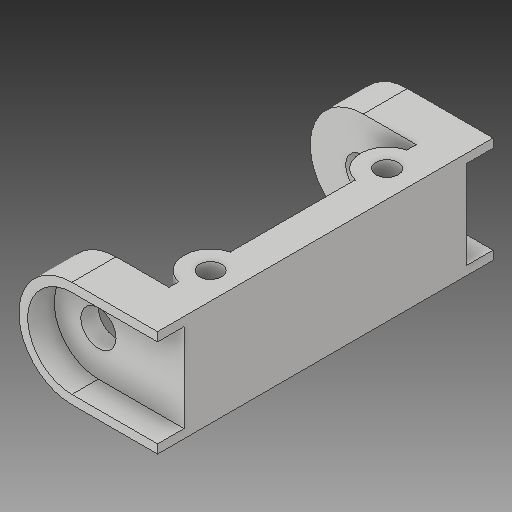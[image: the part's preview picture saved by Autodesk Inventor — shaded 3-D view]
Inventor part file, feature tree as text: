
AUTODESK INVENTOR PART (.ipt)
format: ipt  version: 2019 (Build 230136000, 136)  size: 158,720 bytes
history: native  units: in
note: dims shown in document units (in); Inventor stores cm internally (conversion verified against a paired STEP export)
features: sketch x5, other x3
ambient origin geometry x8: Origin, YZ Plane, XZ Plane, XY Plane, X Axis, Y Axis, Z Axis, Center Point
bodies: Solid1 (feature_tree)
feature tree (8):
  other  "Steering_Arm.ipt"
  other  "Solid1::Steering_Arm.ipt"
  other  "TaggingFeature1"
  sketch  "Sketch1"  dims[d0=0.3937in]
  sketch  "Sketch2"
  sketch  "Sketch3"
  sketch  "Sketch4"
  sketch  "Sketch5"
